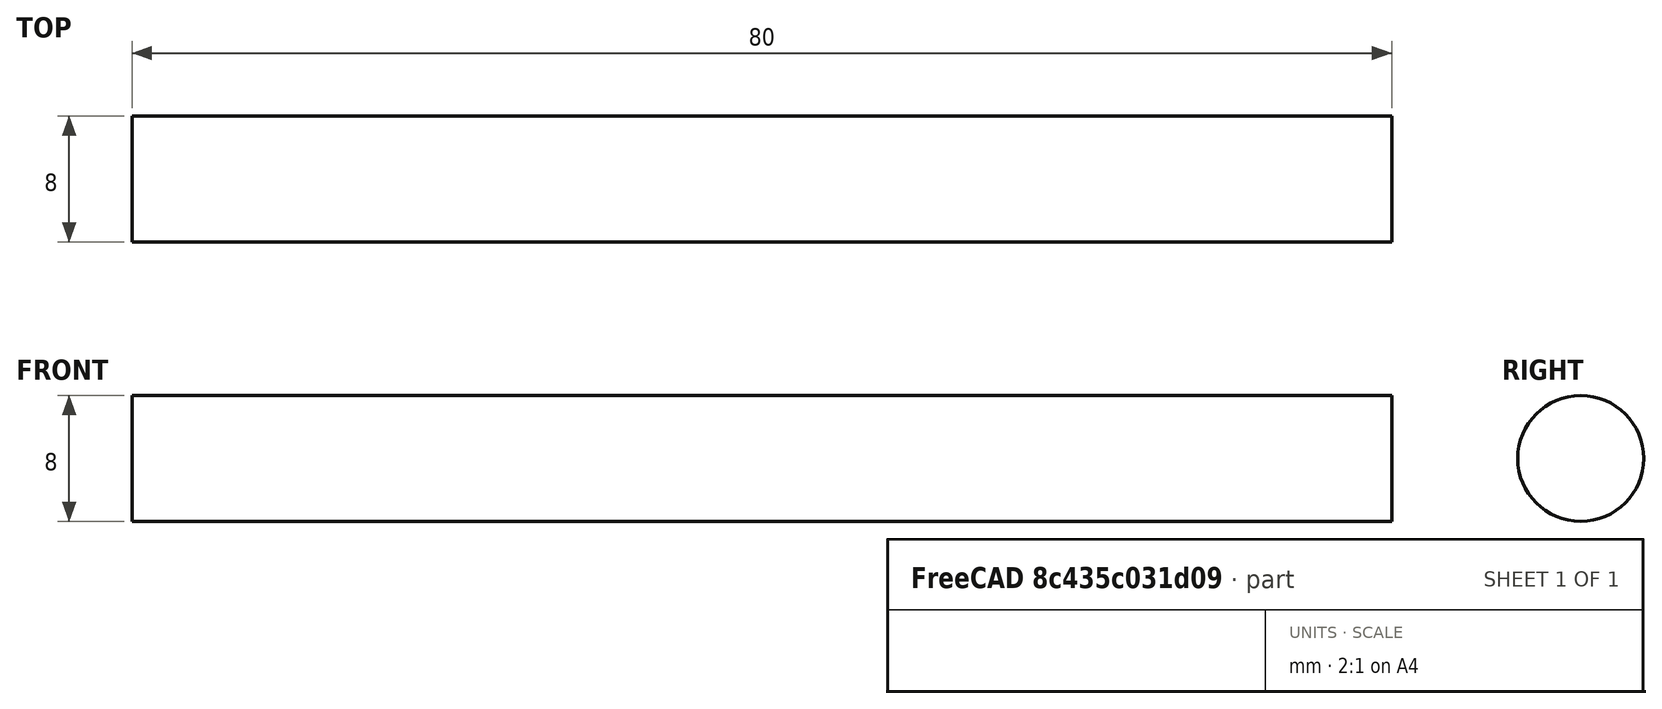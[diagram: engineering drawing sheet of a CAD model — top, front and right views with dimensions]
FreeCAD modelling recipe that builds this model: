
FCSTD DOCUMENT  (FreeCAD 0.18R15441 (Git))
Label: Rod_M8x80mm
License: All rights reserved
LicenseURL: http://en.wikipedia.org/wiki/All_rights_reserved
objects: Sketcher::SketchObject×1, PartDesign::Pad×1, PartDesign::Body×1, App::Part×1
note: 4 computed .brp shape members not serialized (recipe doc carries the construction recipe); baked Part::Feature solids carry a one-line shape summary decoded from their .brp

FEATURE [Sketcher::SketchObject] Sketch  label="RodSketch"
  MapMode = 5
  Placement = pos=(0,0,0) rot=(0.57735,0.57735,0.57735;2.0944rad)
  Support = -> [YZ_Plane001]
  sketch-geometry (1):
    g0: Circle CenterX=0 CenterY=0 CenterZ=0 NormalX=0 NormalY=0 NormalZ=1 AngleXU=0 Radius=4
  constraints (2):
    c: Coincident(g0,g-1)
    c: Radius(g0) = 4
FEATURE [PartDesign::Pad] Pad  label="RodPad"
  Length = 80
  Length2 = 100
  Midplane = true
  Placement = pos=(0,0,0) rot=(0.57735,0.57735,0.57735;2.0944rad)
  Profile = -> Sketch
  Type = 0
FEATURE [PartDesign::Body] Body  label="RodBody"
  Group = -> [Sketch,Pad]
  Origin = -> Origin001
  Tip = -> Pad
FEATURE [App::Part] Part  label="Rod_M8x80_Part"
  Group = -> [Body]
  License = CC BY 3.0
  LicenseURL = http://creativecommons.org/licenses/by/3.0/
  Origin = -> Origin
